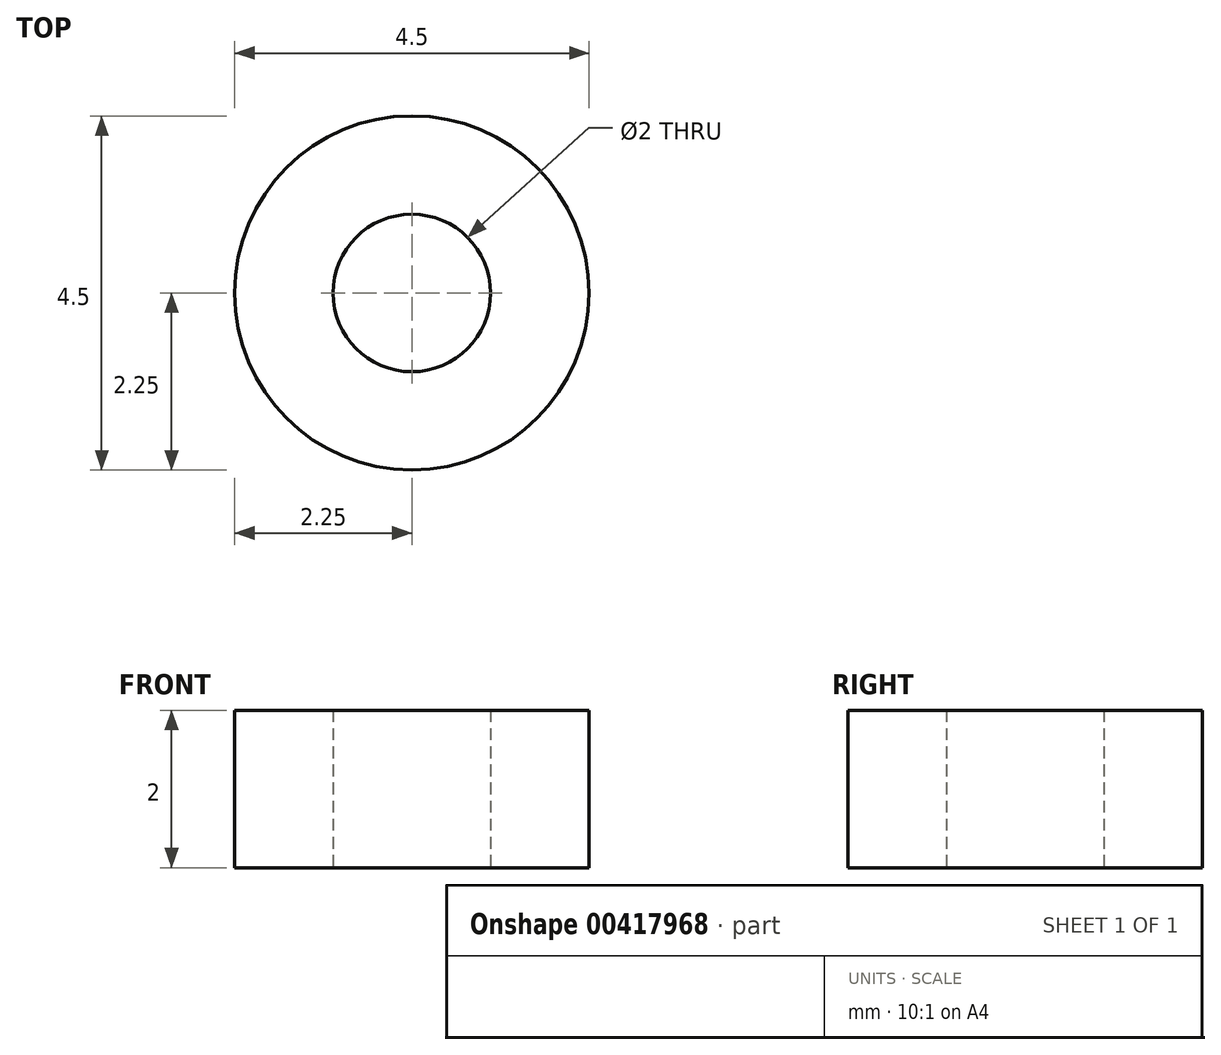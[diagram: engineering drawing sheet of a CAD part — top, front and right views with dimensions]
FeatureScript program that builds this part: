
annotation { "Feature Type Name" : "Feature", "Feature Type Description" : "" }
export const myFeature = defineFeature(function(context is Context, id is Id, definition is map)
    precondition{}
    {
        {
            var Q0;
            Q0=qCreatedBy(makeId("Top.planeOp"),FACE);
            var sketch = newSketch(context, id + "F0", { "sketchPlane" : qUnion([Q0])});
            skCircle(sketch, "E0", {"center": v(0, 0) * mm, "radius": 2.25 * mm});
            skCircle(sketch, "E1", {"center": v(0, 0) * mm, "radius": 1 * mm});
            skSolve(sketch);
        }
        {
            var Q0;
            Q0 = qSketchRegion(id + "F0", true);
            extrude(context, id + "F1", {"entities" : qUnion([Q0]), "depth" : 2 * mm});
        }
    });
